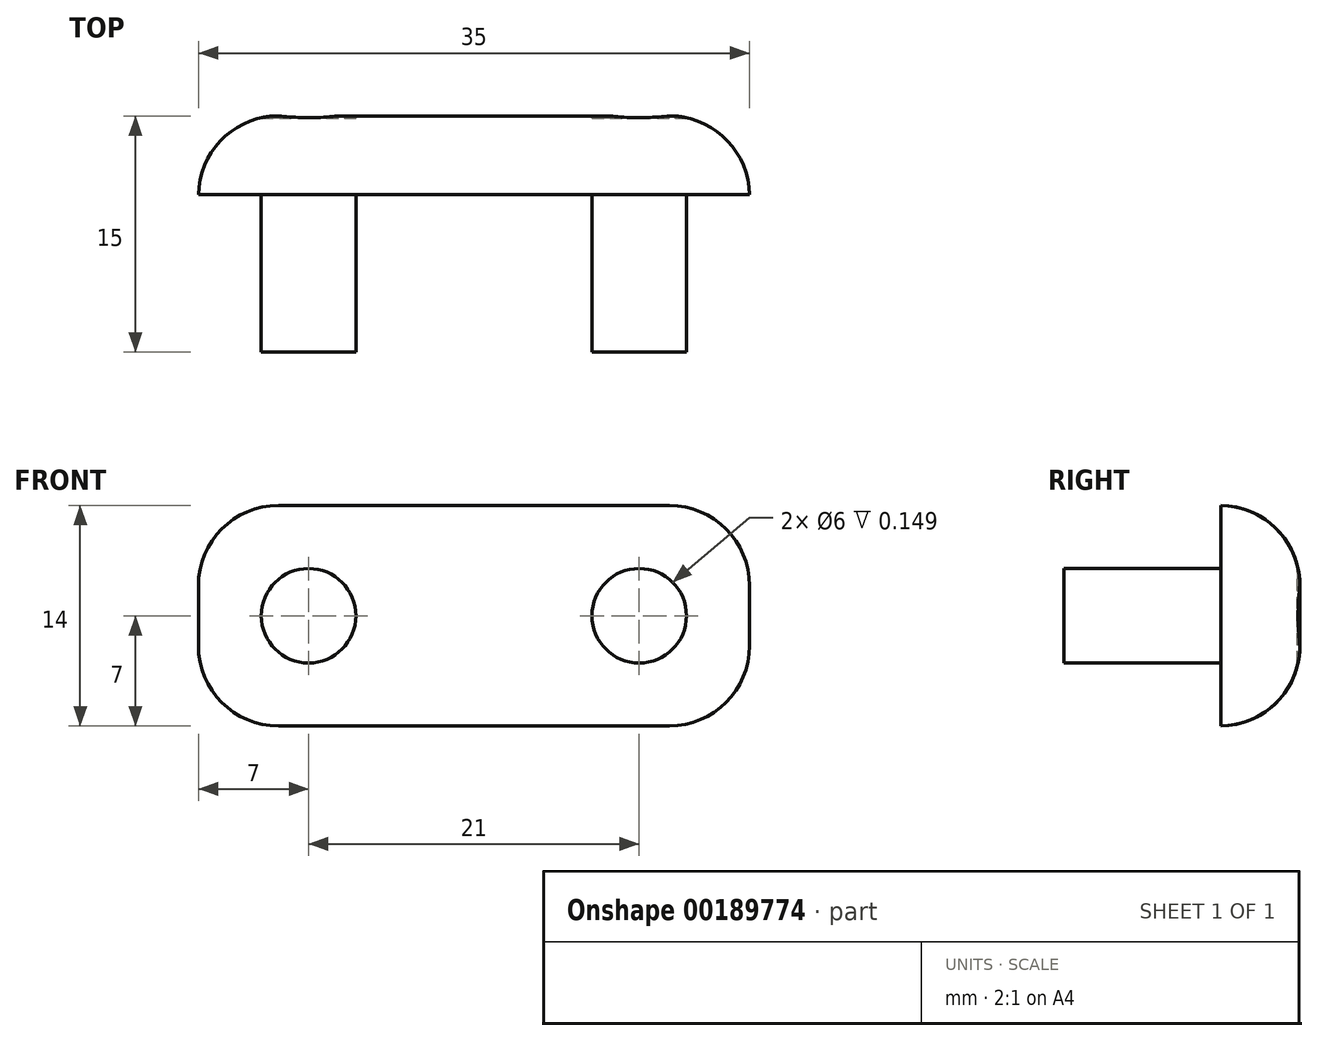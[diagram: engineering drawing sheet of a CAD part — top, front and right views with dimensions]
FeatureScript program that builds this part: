
annotation { "Feature Type Name" : "Feature", "Feature Type Description" : "" }
export const myFeature = defineFeature(function(context is Context, id is Id, definition is map)
    precondition{}
    {
        {
            var Q0;
            Q0=qCreatedBy(makeId("Front.planeOp"),FACE);
            var sketch = newSketch(context, id + "F0", { "sketchPlane" : qUnion([Q0])});
            skLineSegment(sketch, "E0.bottom", {"start": v(0, 0) * mm, "end": v(35, 0) * mm});
            skLineSegment(sketch, "E0.top", {"start": v(0, 14) * mm, "end": v(35, 14) * mm});
            skLineSegment(sketch, "E0.left", {"start": v(0, 0) * mm, "end": v(0, 14) * mm});
            skLineSegment(sketch, "E0.right", {"start": v(35, 0) * mm, "end": v(35, 14) * mm});
            skLineSegment(sketch, "E1", {"start": v(35, 7) * mm, "end": v(0, 7) * mm, "construction": true});
            skLineSegment(sketch, "E2", {"start": v(0, 7) * mm, "end": v(7, 7) * mm, "construction": true});
            skCircle(sketch, "E3", {"center": v(7, 7) * mm, "radius": 3 * mm});
            skLineSegment(sketch, "E4", {"start": v(35, 7) * mm, "end": v(28, 7) * mm, "construction": true});
            skCircle(sketch, "E5", {"center": v(28, 7) * mm, "radius": 3 * mm});
            skSolve(sketch);
        }
        {
            var Q0;
            Q0=makeQuery(id+"F0.imprint","IMPRINT",FACE,{"disambiguationData":[TD([[makeQuery(id+"F0.imprint","IMPRINT",EDGE,{"derivedFrom":sQuery(id+"F0.wireOp",EDGE,"E0.bottom")}),1.0]])]});
            extrude(context, id + "F1", {"entities" : qUnion([Q0]), "depth" : 5 * mm});
        }
        {
            var Q0;
            Q0=makeQuery(id+"F1.opExtrude","SWEPT_EDGE",EDGE,{"disambiguationData":[OSD([sQuery(id+"F0.wireOp",EDGE,"E0.top"),sQuery(id+"F0.wireOp",EDGE,"E0.right")])]});
            var Q1;
            Q1=makeQuery(id+"F1.opExtrude","SWEPT_EDGE",EDGE,{"disambiguationData":[OSD([sQuery(id+"F0.wireOp",EDGE,"E0.bottom"),sQuery(id+"F0.wireOp",EDGE,"E0.right")])]});
            var Q2;
            Q2=makeQuery(id+"F1.opExtrude","SWEPT_EDGE",EDGE,{"disambiguationData":[OSD([sQuery(id+"F0.wireOp",EDGE,"E0.bottom"),sQuery(id+"F0.wireOp",EDGE,"E0.left")])]});
            var Q3;
            Q3=makeQuery(id+"F1.opExtrude","SWEPT_EDGE",EDGE,{"disambiguationData":[OSD([sQuery(id+"F0.wireOp",EDGE,"E0.top"),sQuery(id+"F0.wireOp",EDGE,"E0.left")])]});
            fillet(context, id + "F2", {"entities" : qUnion([Q0, Q1, Q2, Q3]), "radius" : 5.08 * mm, "tangentPropagation" : true, "allowEdgeOverflow" : false});
        }
        {
            var Q0;
            Q0=makeQuery(id+"F1.opExtrude","CAP_FACE",FACE,{"disambiguationData":[OSD([sQuery(id+"F0.wireOp",EDGE,"E0.bottom"),sQuery(id+"F0.wireOp",EDGE,"E0.top"),sQuery(id+"F0.wireOp",EDGE,"E0.left"),sQuery(id+"F0.wireOp",EDGE,"E0.right"),sQuery(id+"F0.wireOp",EDGE,"E3"),sQuery(id+"F0.wireOp",EDGE,"E5")])],"isStart":false});
            var sketch = newSketch(context, id + "F3", { "sketchPlane" : qUnion([Q0])});
            skCircle(sketch, "E6.0", {"center": v(28, 7) * mm, "radius": 3 * mm});
            skCircle(sketch, "E7.0", {"center": v(7, 7) * mm, "radius": 3 * mm});
            skSolve(sketch);
        }
        {
            var Q0;
            Q0=makeQuery(id+"F3.imprint","IMPRINT",FACE,{"disambiguationData":[TD([[makeQuery(id+"F3.imprint","IMPRINT",EDGE,{"derivedFrom":sQuery(id+"F3.wireOp",EDGE,"E6.0")}),1.0]])]});
            var Q1;
            Q1=makeQuery(id+"F3.imprint","IMPRINT",FACE,{"disambiguationData":[TD([[makeQuery(id+"F3.imprint","IMPRINT",EDGE,{"derivedFrom":sQuery(id+"F3.wireOp",EDGE,"E7.0")}),1.0]])]});
            extrude(context, id + "F4", {"entities" : qUnion([Q0, Q1]), "operationType" : NewBodyOperationType.ADD, "depth" : 10 * mm, "hasSecondDirection" : true, "secondDirectionOppositeDirection" : true, "secondDirectionDepth" : 4.85 * mm});
        }
        {
            var Q0;
            Q0=makeQuery(id+"F1.opExtrude","CAP_EDGE",EDGE,{"disambiguationData":[OSD([sQuery(id+"F0.wireOp",EDGE,"E0.top")])],"isStart":true});
            fillet(context, id + "F5", {"entities" : qUnion([Q0]), "radius" : 5.08 * mm, "tangentPropagation" : true, "allowEdgeOverflow" : false});
        }
    });
